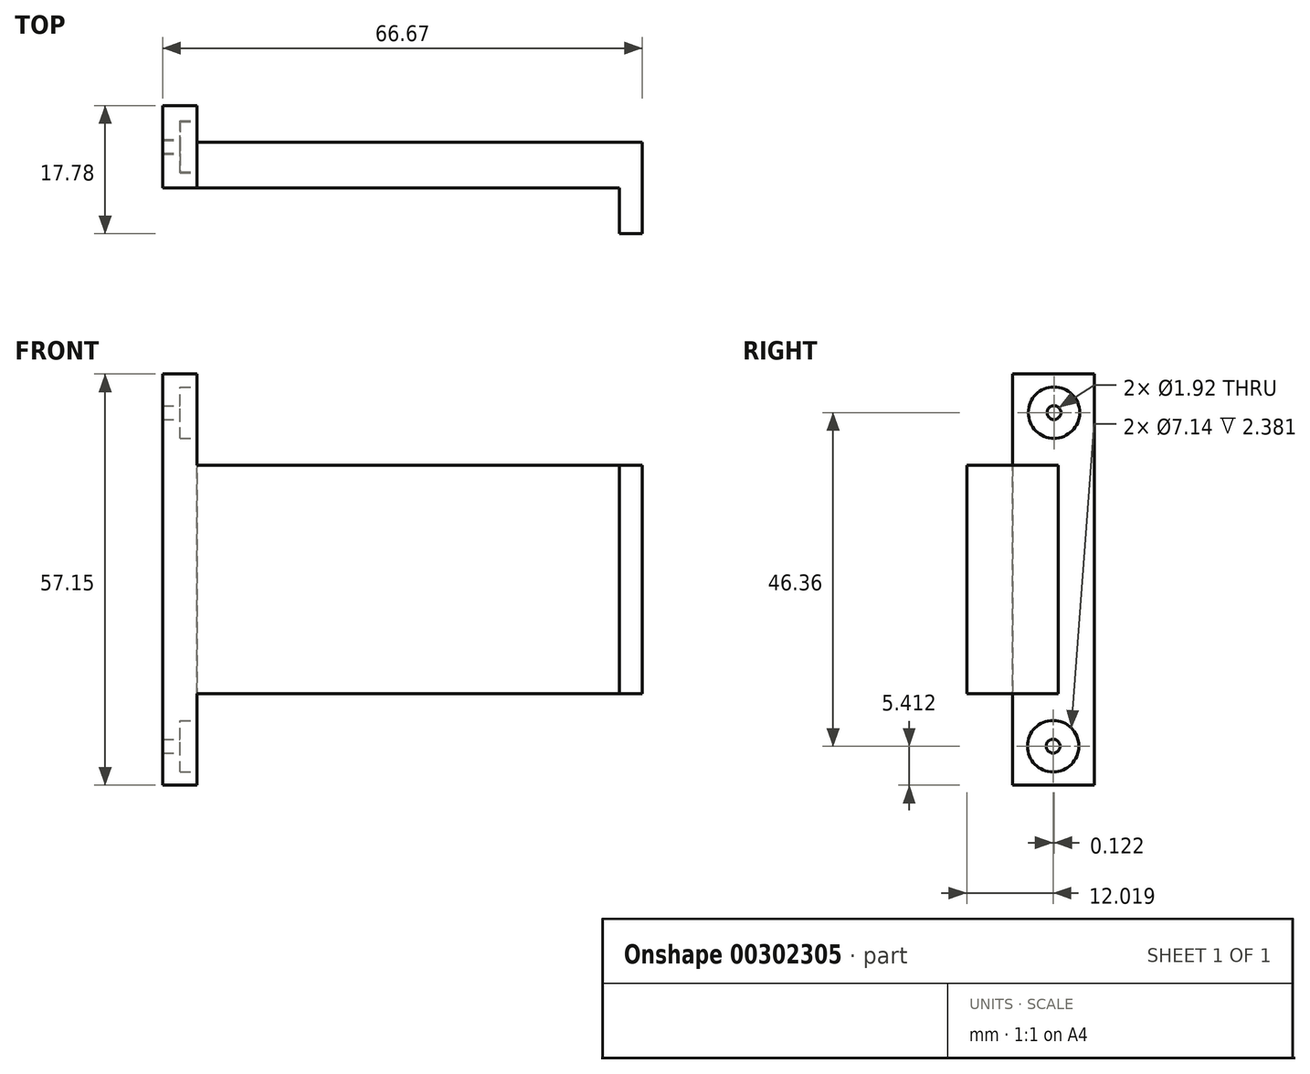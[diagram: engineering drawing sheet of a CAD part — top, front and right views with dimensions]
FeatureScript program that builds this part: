
annotation { "Feature Type Name" : "Feature", "Feature Type Description" : "" }
export const myFeature = defineFeature(function(context is Context, id is Id, definition is map)
    precondition{}
    {
        {
            var Q0;
            Q0=qCreatedBy(makeId("Front.planeOp"),FACE);
            var sketch = newSketch(context, id + "F0", { "sketchPlane" : qUnion([Q0])});
            skLineSegment(sketch, "E0", {"start": v(0, 70.28) * mm, "end": v(0, 38.53) * mm});
            skLineSegment(sketch, "E1", {"start": v(0, 38.53) * mm, "end": v(-63.5, 38.53) * mm});
            skLineSegment(sketch, "E2", {"start": v(-63.5, 38.53) * mm, "end": v(-63.5, 70.28) * mm});
            skLineSegment(sketch, "E3", {"start": v(-63.5, 70.28) * mm, "end": v(0, 70.28) * mm});
            skSolve(sketch);
        }
        {
            var Q0;
            Q0=makeQuery(id+"F0.imprint","IMPRINT",FACE,{"disambiguationData":[TD([[makeQuery(id+"F0.imprint","IMPRINT",EDGE,{"derivedFrom":sQuery(id+"F0.wireOp",EDGE,"E0")}),-1.0]])]});
            extrude(context, id + "F1", {"entities" : qUnion([Q0]), "depth" : 6.35 * mm, "offsetDistance" : 25.4 * mm});
        }
        {
            var Q0;
            Q0=makeQuery(id+"F1.opExtrude","SWEPT_FACE",FACE,{"disambiguationData":[OSD([sQuery(id+"F0.wireOp",EDGE,"E3")])]});
            var sketch = newSketch(context, id + "F2", { "sketchPlane" : qUnion([Q0])});
            skLineSegment(sketch, "E4", {"start": v(-63.5, -6.35) * mm, "end": v(-58.74, -6.35) * mm});
            skLineSegment(sketch, "E5", {"start": v(-58.74, -6.35) * mm, "end": v(-58.74, 0) * mm});
            skLineSegment(sketch, "E6", {"start": v(-58.74, 0) * mm, "end": v(-63.5, 0) * mm});
            skLineSegment(sketch, "E7", {"start": v(-63.5, 0) * mm, "end": v(-63.5, -6.35) * mm});
            skSolve(sketch);
        }
        {
            var Q0;
            Q0=makeQuery(id+"F2.imprint","IMPRINT",FACE,{"disambiguationData":[TD([[makeQuery(id+"F2.imprint","IMPRINT",EDGE,{"derivedFrom":sQuery(id+"F2.wireOp",EDGE,"E4")}),1.0]])]});
            extrude(context, id + "F3", {"entities" : qUnion([Q0]), "operationType" : NewBodyOperationType.ADD, "depth" : 12.7 * mm, "offsetDistance" : 25.4 * mm});
        }
        {
            var Q0;
            Q0=makeQuery(id+"F1.opExtrude","SWEPT_FACE",FACE,{"disambiguationData":[OSD([sQuery(id+"F0.wireOp",EDGE,"E1")])]});
            var sketch = newSketch(context, id + "F4", { "sketchPlane" : qUnion([Q0])});
            skLineSegment(sketch, "E8", {"start": v(-63.5, 6.35) * mm, "end": v(-58.74, 6.35) * mm});
            skLineSegment(sketch, "E9", {"start": v(-58.74, 6.35) * mm, "end": v(-58.74, 0) * mm});
            skLineSegment(sketch, "E10", {"start": v(-63.5, 0) * mm, "end": v(-58.74, 0) * mm});
            skLineSegment(sketch, "E11", {"start": v(-63.5, 0) * mm, "end": v(-63.5, 6.35) * mm});
            skSolve(sketch);
        }
        {
            var Q0;
            Q0 = qSketchRegion(id + "F4", true);
            extrude(context, id + "F5", {"entities" : qUnion([Q0]), "operationType" : NewBodyOperationType.ADD, "depth" : 12.7 * mm, "offsetDistance" : 25.4 * mm});
        }
        {
            var Q0;
            Q0=makeQuery(id+"F5.boolean.opBoolean","MERGE",FACE,{"derivedFrom":[makeQuery(id+"F3.boolean.opBoolean","MERGE",FACE,{"derivedFrom":[makeQuery(id+"F1.opExtrude","CAP_FACE",FACE,{"disambiguationData":[OSD([sQuery(id+"F0.wireOp",EDGE,"E0"),sQuery(id+"F0.wireOp",EDGE,"E1"),sQuery(id+"F0.wireOp",EDGE,"E2"),sQuery(id+"F0.wireOp",EDGE,"E3")])],"isStart":true}),makeQuery(id+"F3.opExtrude","SWEPT_FACE",FACE,{"disambiguationData":[OSD([sQuery(id+"F2.wireOp",EDGE,"E6")])]})]}),makeQuery(id+"F5.opExtrude","SWEPT_FACE",FACE,{"disambiguationData":[OSD([sQuery(id+"F4.wireOp",EDGE,"E10")])]})]});
            var sketch = newSketch(context, id + "F6", { "sketchPlane" : qUnion([Q0])});
            skLineSegment(sketch, "E12", {"start": v(58.74, 70.28) * mm, "end": v(63.5, 70.28) * mm});
            skLineSegment(sketch, "E13", {"start": v(63.5, 70.28) * mm, "end": v(63.5, 82.98) * mm});
            skLineSegment(sketch, "E14", {"start": v(63.5, 82.98) * mm, "end": v(58.74, 82.98) * mm});
            skLineSegment(sketch, "E15", {"start": v(58.74, 82.98) * mm, "end": v(58.74, 70.28) * mm});
            skSolve(sketch);
        }
        {
            var Q0;
            Q0=makeQuery(id+"F6.imprint","IMPRINT",FACE,{"disambiguationData":[TD([[makeQuery(id+"F6.imprint","IMPRINT",EDGE,{"derivedFrom":sQuery(id+"F6.wireOp",EDGE,"E12")}),1.0]])]});
            extrude(context, id + "F7", {"entities" : qUnion([Q0]), "operationType" : NewBodyOperationType.ADD, "depth" : 5.08 * mm, "offsetDistance" : 25.4 * mm});
        }
        {
            var Q0;
            Q0=makeQuery(id+"F7.boolean.opBoolean","MERGE",FACE,{"derivedFrom":[makeQuery(id+"F3.opExtrude","SWEPT_FACE",FACE,{"disambiguationData":[OSD([sQuery(id+"F2.wireOp",EDGE,"E5")])]}),makeQuery(id+"F7.opExtrude","SWEPT_FACE",FACE,{"disambiguationData":[OSD([sQuery(id+"F6.wireOp",EDGE,"E15")])]})]});
            var sketch = newSketch(context, id + "F8", { "sketchPlane" : qUnion([Q0])});
            skCircle(sketch, "E16", {"center": v(-0.56, 77.6) * mm, "radius": 3.57 * mm});
            skCircle(sketch, "E17", {"center": v(-0.56, 77.6) * mm, "radius": 0.96 * mm});
            skSolve(sketch);
        }
        {
            var Q0;
            Q0=makeQuery(id+"F8.imprint","IMPRINT",FACE,{"disambiguationData":[TD([[makeQuery(id+"F8.imprint","IMPRINT",EDGE,{"derivedFrom":sQuery(id+"F8.wireOp",EDGE,"E16")}),1.0]])]});
            extrude(context, id + "F9", {"entities" : qUnion([Q0]), "operationType" : NewBodyOperationType.REMOVE, "oppositeDirection" : true, "depth" : 2.38 * mm, "offsetDistance" : 25.4 * mm});
        }
        {
            var Q0;
            Q0=makeQuery(id+"F8.imprint","IMPRINT",FACE,{"disambiguationData":[TD([[makeQuery(id+"F8.imprint","IMPRINT",EDGE,{"derivedFrom":sQuery(id+"F8.wireOp",EDGE,"E17")}),1.0]])]});
            extrude(context, id + "F10", {"entities" : qUnion([Q0]), "operationType" : NewBodyOperationType.REMOVE, "oppositeDirection" : true, "depth" : 6.35 * mm, "offsetDistance" : 25.4 * mm});
        }
        {
            var Q0;
            Q0=makeQuery(id+"F5.boolean.opBoolean","MERGE",FACE,{"derivedFrom":[makeQuery(id+"F3.boolean.opBoolean","MERGE",FACE,{"derivedFrom":[makeQuery(id+"F1.opExtrude","CAP_FACE",FACE,{"disambiguationData":[OSD([sQuery(id+"F0.wireOp",EDGE,"E0"),sQuery(id+"F0.wireOp",EDGE,"E1"),sQuery(id+"F0.wireOp",EDGE,"E2"),sQuery(id+"F0.wireOp",EDGE,"E3")])],"isStart":true}),makeQuery(id+"F3.opExtrude","SWEPT_FACE",FACE,{"disambiguationData":[OSD([sQuery(id+"F2.wireOp",EDGE,"E6")])]})]}),makeQuery(id+"F5.opExtrude","SWEPT_FACE",FACE,{"disambiguationData":[OSD([sQuery(id+"F4.wireOp",EDGE,"E10")])]})]});
            var sketch = newSketch(context, id + "F11", { "sketchPlane" : qUnion([Q0])});
            skLineSegment(sketch, "E18", {"start": v(58.74, 38.53) * mm, "end": v(63.5, 38.53) * mm});
            skLineSegment(sketch, "E19", {"start": v(63.5, 25.83) * mm, "end": v(63.5, 38.53) * mm});
            skLineSegment(sketch, "E20", {"start": v(58.74, 38.53) * mm, "end": v(58.74, 25.83) * mm});
            skLineSegment(sketch, "E21", {"start": v(58.74, 25.83) * mm, "end": v(63.5, 25.83) * mm});
            skSolve(sketch);
        }
        {
            var Q0;
            Q0=makeQuery(id+"F11.imprint","IMPRINT",FACE,{"disambiguationData":[TD([[makeQuery(id+"F11.imprint","IMPRINT",EDGE,{"derivedFrom":sQuery(id+"F11.wireOp",EDGE,"E18")}),-1.0]])]});
            extrude(context, id + "F12", {"entities" : qUnion([Q0]), "operationType" : NewBodyOperationType.ADD, "depth" : 5.08 * mm, "offsetDistance" : 25.4 * mm});
        }
        {
            var Q0;
            Q0=makeQuery(id+"F12.boolean.opBoolean","MERGE",FACE,{"derivedFrom":[makeQuery(id+"F5.opExtrude","SWEPT_FACE",FACE,{"disambiguationData":[OSD([sQuery(id+"F4.wireOp",EDGE,"E9")])]}),makeQuery(id+"F12.opExtrude","SWEPT_FACE",FACE,{"disambiguationData":[OSD([sQuery(id+"F11.wireOp",EDGE,"E20")])]})]});
            var sketch = newSketch(context, id + "F13", { "sketchPlane" : qUnion([Q0])});
            skCircle(sketch, "E22", {"center": v(-0.68, 31.24) * mm, "radius": 3.57 * mm});
            skCircle(sketch, "E23", {"center": v(-0.68, 31.24) * mm, "radius": 0.96 * mm});
            skSolve(sketch);
        }
        {
            var Q0;
            Q0=makeQuery(id+"F13.imprint","IMPRINT",FACE,{"disambiguationData":[TD([[makeQuery(id+"F13.imprint","IMPRINT",EDGE,{"derivedFrom":sQuery(id+"F13.wireOp",EDGE,"E23")}),1.0]])]});
            extrude(context, id + "F14", {"entities" : qUnion([Q0]), "operationType" : NewBodyOperationType.REMOVE, "oppositeDirection" : true, "depth" : 6.35 * mm, "offsetDistance" : 25.4 * mm});
        }
        {
            var Q0;
            Q0=makeQuery(id+"F13.imprint","IMPRINT",FACE,{"disambiguationData":[TD([[makeQuery(id+"F13.imprint","IMPRINT",EDGE,{"derivedFrom":sQuery(id+"F13.wireOp",EDGE,"E22")}),1.0]])]});
            extrude(context, id + "F15", {"entities" : qUnion([Q0]), "operationType" : NewBodyOperationType.REMOVE, "oppositeDirection" : true, "depth" : 2.38 * mm, "offsetDistance" : 25.4 * mm});
        }
        {
            var Q0;
            Q0=makeQuery(id+"F7.opExtrude","SWEPT_FACE",FACE,{"disambiguationData":[OSD([sQuery(id+"F6.wireOp",EDGE,"E12")])]});
            extrude(context, id + "F16", {"entities" : qUnion([Q0]), "operationType" : NewBodyOperationType.ADD, "depth" : 31.75 * mm, "offsetDistance" : 25.4 * mm});
        }
        {
            var Q0;
            Q0=makeQuery(id+"F1.opExtrude","SWEPT_FACE",FACE,{"disambiguationData":[OSD([sQuery(id+"F0.wireOp",EDGE,"E0")])]});
            extrude(context, id + "F17", {"entities" : qUnion([Q0]), "operationType" : NewBodyOperationType.ADD, "depth" : 3.17 * mm, "offsetDistance" : 25.4 * mm});
        }
        {
            var Q0;
            {var subQ0=sQuery(id+"F0.wireOp",EDGE,"E0");Q0=makeQuery(id+"F17.boolean.opBoolean","MERGE",FACE,{"derivedFrom":[makeQuery(id+"F5.boolean.opBoolean","MERGE",FACE,{"derivedFrom":[makeQuery(id+"F3.boolean.opBoolean","MERGE",FACE,{"derivedFrom":[makeQuery(id+"F1.opExtrude","CAP_FACE",FACE,{"disambiguationData":[OSD([subQ0,sQuery(id+"F0.wireOp",EDGE,"E1"),sQuery(id+"F0.wireOp",EDGE,"E2"),sQuery(id+"F0.wireOp",EDGE,"E3")])],"isStart":false}),makeQuery(id+"F3.opExtrude","SWEPT_FACE",FACE,{"disambiguationData":[OSD([sQuery(id+"F2.wireOp",EDGE,"E4")])]})]}),makeQuery(id+"F5.opExtrude","SWEPT_FACE",FACE,{"disambiguationData":[OSD([sQuery(id+"F4.wireOp",EDGE,"E8")])]})]}),makeQuery(id+"F17.opExtrude","SWEPT_FACE",FACE,{"disambiguationData":[OSD([subQ0]),TDD([makeQuery(id+"F1.opExtrude","CAP_EDGE",EDGE,{"disambiguationData":[OSD([subQ0])],"isStart":false})])]})]});}
            var sketch = newSketch(context, id + "F18", { "sketchPlane" : qUnion([Q0])});
            skLineSegment(sketch, "E24", {"start": v(0, 70.28) * mm, "end": v(0, 38.53) * mm});
            skLineSegment(sketch, "E25", {"start": v(0, 38.53) * mm, "end": v(3.18, 38.53) * mm});
            skLineSegment(sketch, "E26", {"start": v(3.18, 38.53) * mm, "end": v(3.18, 70.28) * mm});
            skLineSegment(sketch, "E27", {"start": v(3.18, 70.28) * mm, "end": v(0, 70.28) * mm});
            skSolve(sketch);
        }
        {
            var Q0;
            Q0=makeQuery(id+"F18.imprint","IMPRINT",FACE,{"disambiguationData":[TD([[makeQuery(id+"F18.imprint","IMPRINT",EDGE,{"derivedFrom":sQuery(id+"F18.wireOp",EDGE,"E24")}),1.0]])]});
            extrude(context, id + "F19", {"entities" : qUnion([Q0]), "operationType" : NewBodyOperationType.ADD, "depth" : 6.35 * mm, "offsetDistance" : 25.4 * mm});
        }
    });
